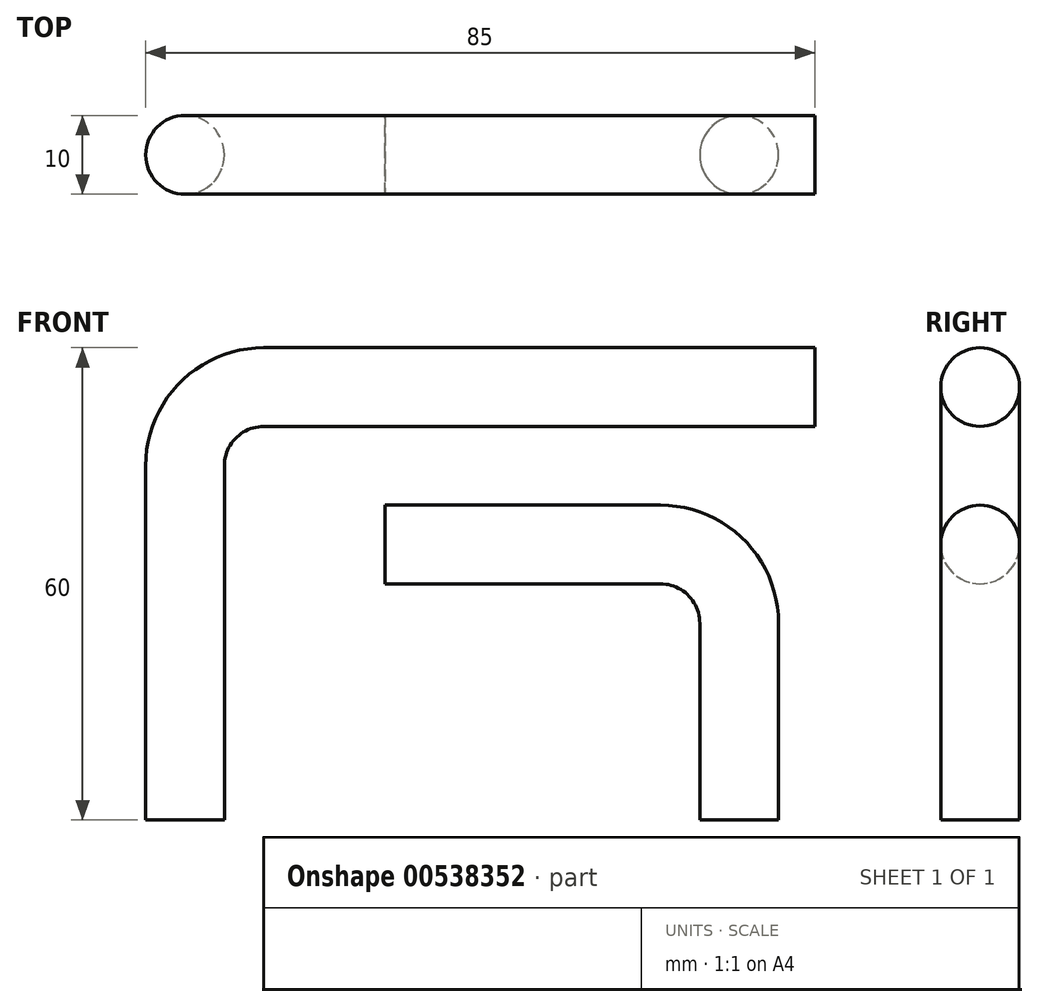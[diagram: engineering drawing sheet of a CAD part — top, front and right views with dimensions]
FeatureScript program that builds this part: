
annotation { "Feature Type Name" : "Feature", "Feature Type Description" : "" }
export const myFeature = defineFeature(function(context is Context, id is Id, definition is map)
    precondition{}
    {
        {
            var Q0;
            Q0=qCreatedBy(makeId("Front.planeOp"),FACE);
            var sketch = newSketch(context, id + "F0", { "sketchPlane" : qUnion([Q0])});
            skLineSegment(sketch, "E0", {"start": v(0, 0) * mm, "end": v(0, 45) * mm});
            skLineSegment(sketch, "E1", {"start": v(10, 55) * mm, "end": v(80, 55) * mm});
            skPoint(sketch, "E2.visualSharp", {"position": v(0, 55) * mm});
            skArc(sketch, "E2.filletArc", {"start": v(10, 55) * mm, "mid": v(2.93, 52.07) * mm, "end": v(0, 45) * mm});
            skSolve(sketch);
        }
        {
            var Q0;
            Q0=qCreatedBy(makeId("Top.planeOp"),FACE);
            var sketch = newSketch(context, id + "F1", { "sketchPlane" : qUnion([Q0])});
            skCircle(sketch, "E3", {"center": v(0, 0) * mm, "radius": 5 * mm});
            skSolve(sketch);
        }
        {
            var Q0;
            Q0=makeQuery(id+"F1.imprint","IMPRINT",FACE,{"disambiguationData":[TD([[makeQuery(id+"F1.imprint","IMPRINT",EDGE,{"derivedFrom":sQuery(id+"F1.wireOp",EDGE,"E3")}),1.0]])]});
            var Q1;
            Q1=sQuery(id+"F0.wireOp",EDGE,"E0");
            var Q2;
            Q2=sQuery(id+"F0.wireOp",EDGE,"E2.filletArc");
            var Q3;
            Q3=sQuery(id+"F0.wireOp",EDGE,"E1");
            sweep(context, id + "F2", {"profiles" : qUnion([Q0]), "path" : qUnion([Q1, Q2, Q3])});
        }
        {
            var Q0;
            Q0=qCreatedBy(makeId("Front.planeOp"),FACE);
            var sketch = newSketch(context, id + "F3", { "sketchPlane" : qUnion([Q0])});
            skLineSegment(sketch, "E4", {"start": v(70.39, 0) * mm, "end": v(70.39, 25) * mm});
            skLineSegment(sketch, "E5", {"start": v(60.39, 35) * mm, "end": v(25.39, 35) * mm});
            skPoint(sketch, "E6.visualSharp", {"position": v(70.39, 35) * mm});
            skArc(sketch, "E6.filletArc", {"start": v(70.39, 25) * mm, "mid": v(67.46, 32.07) * mm, "end": v(60.39, 35) * mm});
            skSolve(sketch);
        }
        {
            var Q0;
            Q0=qCreatedBy(makeId("Top.planeOp"),FACE);
            var sketch = newSketch(context, id + "F4", { "sketchPlane" : qUnion([Q0])});
            skCircle(sketch, "E7", {"center": v(70.39, 0) * mm, "radius": 5 * mm});
            skSolve(sketch);
        }
        {
            var Q0;
            Q0=makeQuery(id+"F4.imprint","IMPRINT",FACE,{"disambiguationData":[TD([[makeQuery(id+"F4.imprint","IMPRINT",EDGE,{"derivedFrom":sQuery(id+"F4.wireOp",EDGE,"E7")}),1.0]])]});
            var Q1;
            Q1=sQuery(id+"F3.wireOp",EDGE,"E4");
            var Q2;
            Q2=sQuery(id+"F3.wireOp",EDGE,"E6.filletArc");
            var Q3;
            Q3=sQuery(id+"F3.wireOp",EDGE,"E5");
            sweep(context, id + "F5", {"profiles" : qUnion([Q0]), "path" : qUnion([Q1, Q2, Q3])});
        }
    });
